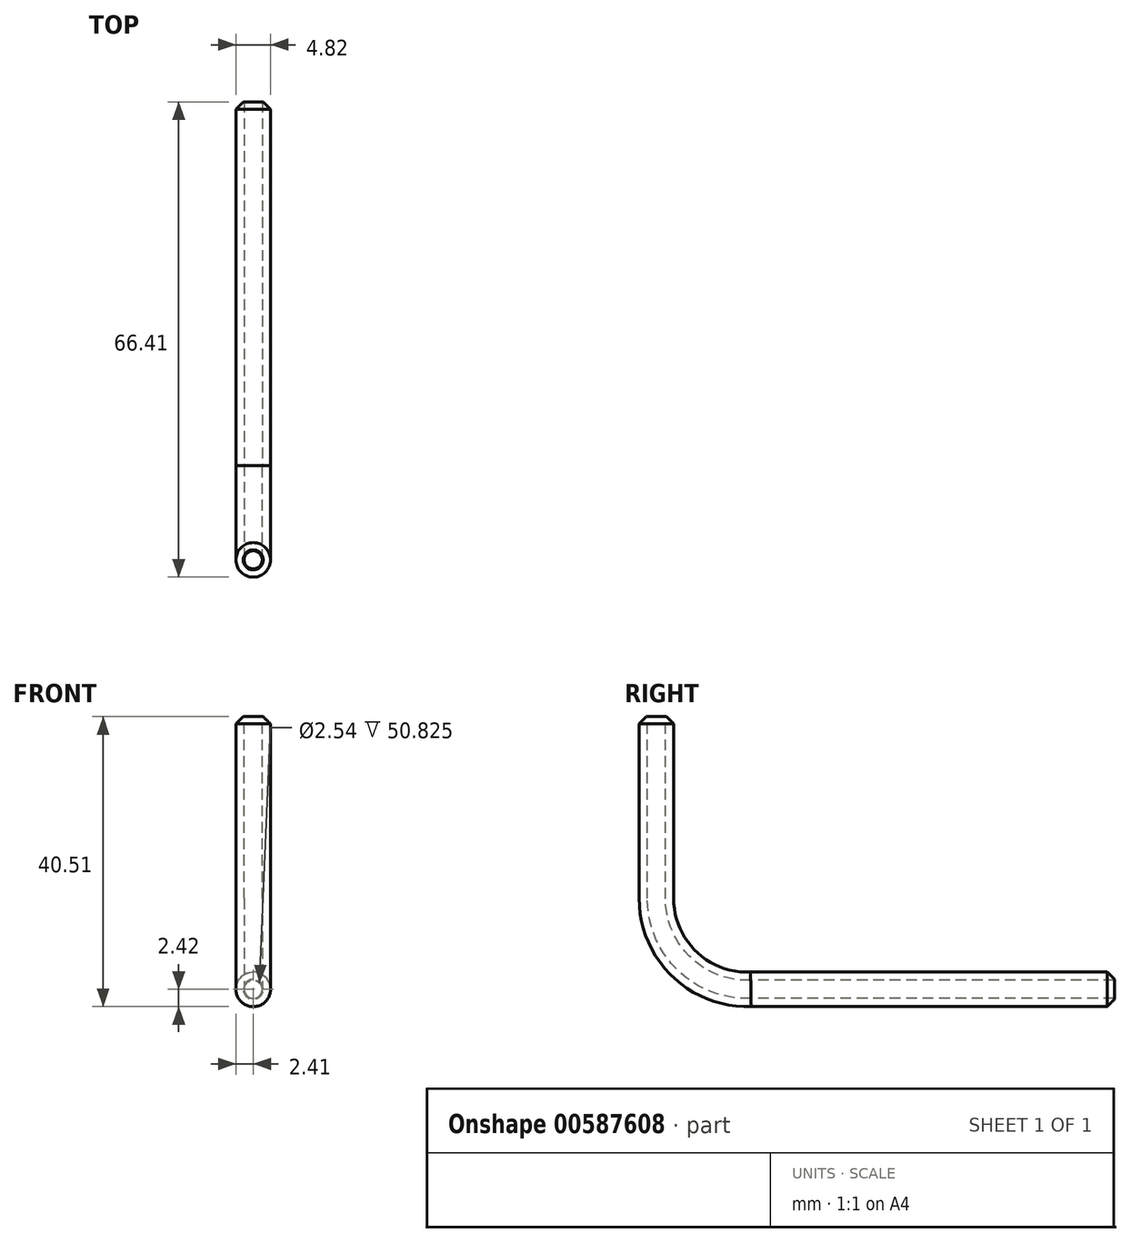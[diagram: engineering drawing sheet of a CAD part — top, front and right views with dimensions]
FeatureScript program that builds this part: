
annotation { "Feature Type Name" : "Feature", "Feature Type Description" : "" }
export const myFeature = defineFeature(function(context is Context, id is Id, definition is map)
    precondition{}
    {
        {
            var Q0;
            Q0=qCreatedBy(makeId("Right.planeOp"),FACE);
            var sketch = newSketch(context, id + "F0", { "sketchPlane" : qUnion([Q0])});
            skLineSegment(sketch, "E0", {"start": v(0, 25.4) * mm, "end": v(0, 0) * mm});
            skArc(sketch, "E1", {"start": v(0, 0) * mm, "mid": v(3.9, -9.16) * mm, "end": v(13.2, -12.7) * mm});
            skLineSegment(sketch, "E2", {"start": v(13.2, -12.7) * mm, "end": v(64, -12.7) * mm});
            skSolve(sketch);
        }
        {
            var Q0;
            Q0=qCreatedBy(makeId("Top.planeOp"),FACE);
            var sketch = newSketch(context, id + "F1", { "sketchPlane" : qUnion([Q0])});
            skCircle(sketch, "E3", {"center": v(0, 0) * mm, "radius": 2.41 * mm});
            skCircle(sketch, "E4", {"center": v(0, 0) * mm, "radius": 1.27 * mm});
            skSolve(sketch);
        }
        {
            var Q0;
            Q0=makeQuery(id+"F1.imprint","IMPRINT",FACE,{"disambiguationData":[TD([[makeQuery(id+"F1.imprint","IMPRINT",EDGE,{"derivedFrom":sQuery(id+"F1.wireOp",EDGE,"E3")}),1.0]])]});
            var Q1;
            Q1=sQuery(id+"F0.wireOp",EDGE,"E0");
            var Q2;
            Q2=sQuery(id+"F0.wireOp",EDGE,"E1");
            var Q3;
            Q3=sQuery(id+"F0.wireOp",EDGE,"E2");
            sweep(context, id + "F2", {"profiles" : qUnion([Q0]), "path" : qUnion([Q1, Q2, Q3])});
        }
        {
            var Q0;
            Q0=makeQuery(id+"F2.opSweep","CAP_EDGE",EDGE,{"disambiguationData":[OSD([sQuery(id+"F0.wireOp",VERTEX,"E0.start"),sQuery(id+"F1.wireOp",EDGE,"E3")])],"isStart":false});
            chamfer(context, id + "F3", {"entities" : qUnion([Q0]), "width" : 1.02 * mm, "tangentPropagation" : true});
        }
        {
            var Q0;
            Q0=makeQuery(id+"F2.opSweep","CAP_EDGE",EDGE,{"disambiguationData":[OSD([sQuery(id+"F0.wireOp",VERTEX,"E2.end"),sQuery(id+"F1.wireOp",EDGE,"E3")])],"isStart":true});
            chamfer(context, id + "F4", {"entities" : qUnion([Q0]), "width" : 1.02 * mm, "tangentPropagation" : true});
        }
    });
